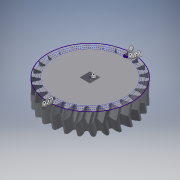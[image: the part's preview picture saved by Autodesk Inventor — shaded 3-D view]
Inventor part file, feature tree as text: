
AUTODESK INVENTOR PART (.ipt)
format: ipt  version: 2017 (Build 210142000, 142)  size: 1,043,456 bytes
history: native  units: mm
features: sketch x3, extrude x3, pattern_circular x2, helix x2, projected_geometry x1
ambient origin geometry x8: Origin, YZ Plane, XZ Plane, XY Plane, X Axis, Y Axis, Z Axis, Center Point
bodies: Solid1 (feature_tree)
feature tree (11):
  sketch  "Sketch1"  dims[d0=20.0mm d1=0.0mm]
  extrude  "Extrusion1"  TaperAngle=0.0deg  [1 undecoded]
  extrude  "Extrusion2"  Depth=260.0mm TaperAngle=360.0deg
  pattern_circular  "Circular Pattern1"  [2 undecoded]
  extrude  "Extrusion3"  Depth=260.0mm TaperAngle=360.0deg
  helix  "Coil1"  [1 undecoded]
  helix  "Coil2"  [1 undecoded]
  pattern_circular  "Circular Pattern2"  [2 undecoded]
  sketch  "Sketch2"  dims[d2=10.0mm d3=0.0mm d4=260.0mm d5=360.0deg]
  sketch  "Sketch3"  dims[d7=9.525mm d8=10.0mm d9=0.0mm d10=10.0mm d11=10.0mm d12=0.1mm d13=0.0mm d14=90.0deg d15=90.0deg d16=0.0mm d17=0.0mm d18=10.0mm d19=10.0mm d20=0.1mm d21=0.0mm d22=90.0deg d23=90.0deg d24=0.0mm d25=0.0mm d26=260.0mm d27=360.0deg]
  projected_geometry  "Projected Loop1"
note: 7 required parameter values undecoded (feature->parameter linkage not recoverable at this tier; creation-order binding heuristic only, values carry confidence <= 0.55)
